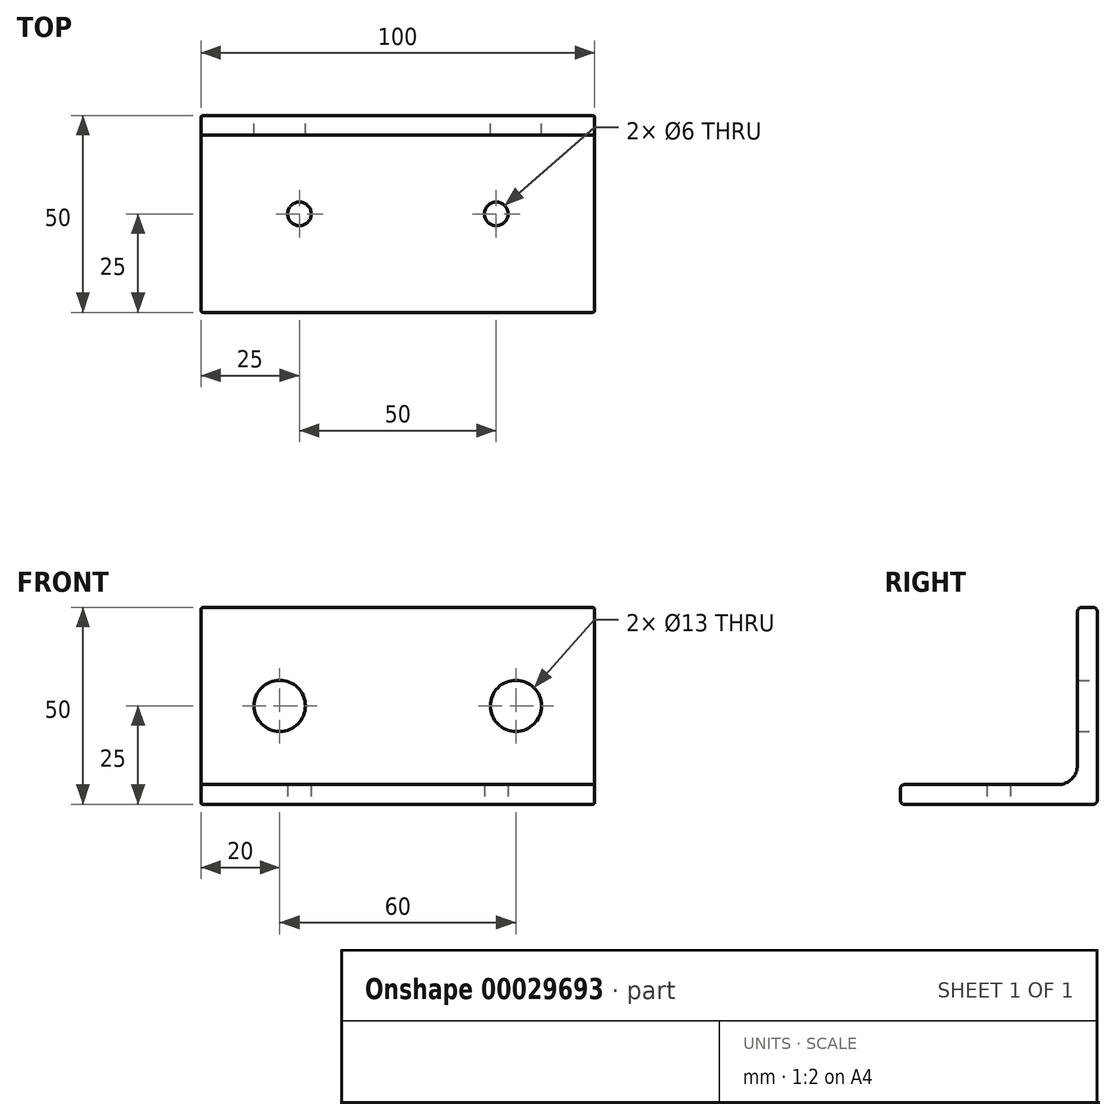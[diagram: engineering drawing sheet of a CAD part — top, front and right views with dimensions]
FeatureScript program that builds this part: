
annotation { "Feature Type Name" : "Feature", "Feature Type Description" : "" }
export const myFeature = defineFeature(function(context is Context, id is Id, definition is map)
    precondition{}
    {
        {
            var Q0;
            Q0=qCreatedBy(makeId("Right.planeOp"),FACE);
            var sketch = newSketch(context, id + "F0", { "sketchPlane" : qUnion([Q0])});
            skLineSegment(sketch, "E0", {"start": v(-49, 0) * mm, "end": v(-1, 0) * mm});
            skLineSegment(sketch, "E1", {"start": v(0, 1) * mm, "end": v(0, 49) * mm});
            skLineSegment(sketch, "E2", {"start": v(-1, 50) * mm, "end": v(-4, 50) * mm});
            skLineSegment(sketch, "E3", {"start": v(-5, 49) * mm, "end": v(-5, 10) * mm});
            skLineSegment(sketch, "E4", {"start": v(-10, 5) * mm, "end": v(-49, 5) * mm});
            skLineSegment(sketch, "E5", {"start": v(-50, 4) * mm, "end": v(-50, 1) * mm});
            skPoint(sketch, "E6.visualSharp", {"position": v(-5, 5) * mm});
            skArc(sketch, "E6.filletArc", {"start": v(-10, 5) * mm, "mid": v(-6.46, 6.46) * mm, "end": v(-5, 10) * mm});
            skPoint(sketch, "E7.visualSharp", {"position": v(0, 50) * mm});
            skArc(sketch, "E7.filletArc", {"start": v(0, 49) * mm, "mid": v(-0.3, 49.7) * mm, "end": v(-1, 50) * mm});
            skPoint(sketch, "E8.visualSharp", {"position": v(-5, 50) * mm});
            skArc(sketch, "E8.filletArc", {"start": v(-4, 50) * mm, "mid": v(-4.7, 49.7) * mm, "end": v(-5, 49) * mm});
            skPoint(sketch, "E9.visualSharp", {"position": v(-50, 5) * mm});
            skArc(sketch, "E9.filletArc", {"start": v(-49, 5) * mm, "mid": v(-49.7, 4.7) * mm, "end": v(-50, 4) * mm});
            skPoint(sketch, "E10.visualSharp", {"position": v(-50, 0) * mm});
            skArc(sketch, "E10.filletArc", {"start": v(-50, 1) * mm, "mid": v(-49.7, 0.3) * mm, "end": v(-49, 0) * mm});
            skPoint(sketch, "E11.visualSharp", {"position": v(0, 0) * mm});
            skArc(sketch, "E11.filletArc", {"start": v(-1, 0) * mm, "mid": v(-0.3, 0.3) * mm, "end": v(0, 1) * mm});
            skSolve(sketch);
        }
        {
            var Q0;
            Q0=qSketchRegion(id+"F0",true);
            extrude(context, id + "F1", {"entities" : qUnion([Q0]), "endBound" : BoundingType.SYMMETRIC, "depth" : 100 * mm});
        }
        {
            var Q0;
            Q0=makeQuery(id+"F1.opExtrude","SWEPT_FACE",FACE,{"disambiguationData":[OSD([sQuery(id+"F0.wireOp",EDGE,"E1")])]});
            var sketch = newSketch(context, id + "F2", { "sketchPlane" : qUnion([Q0])});
            skLineSegment(sketch, "E12.0", {"start": v(-50, 50) * mm, "end": v(50, 50) * mm, "construction": true});
            skLineSegment(sketch, "E12.1", {"start": v(-50, 0) * mm, "end": v(50, 0) * mm, "construction": true});
            skLineSegment(sketch, "E13", {"start": v(-50, 25) * mm, "end": v(-30, 25) * mm, "construction": true});
            skLineSegment(sketch, "E14", {"start": v(50, 25) * mm, "end": v(30, 25) * mm, "construction": true});
            skCircle(sketch, "E15", {"center": v(-30, 25) * mm, "radius": 6.5 * mm});
            skCircle(sketch, "E16", {"center": v(30, 25) * mm, "radius": 6.5 * mm});
            skSolve(sketch);
        }
        {
            var Q0;
            Q0=makeQuery(id+"F2.imprint","IMPRINT",FACE,{"disambiguationData":[TD([[makeQuery(id+"F2.imprint","IMPRINT",EDGE,{"derivedFrom":sQuery(id+"F2.wireOp",EDGE,"E15")}),1.0]])]});
            var Q1;
            Q1=makeQuery(id+"F2.imprint","IMPRINT",FACE,{"disambiguationData":[TD([[makeQuery(id+"F2.imprint","IMPRINT",EDGE,{"derivedFrom":sQuery(id+"F2.wireOp",EDGE,"E16")}),1.0]])]});
            extrude(context, id + "F3", {"entities" : qUnion([Q0, Q1]), "operationType" : NewBodyOperationType.REMOVE, "endBound" : BoundingType.THROUGH_ALL, "oppositeDirection" : true, "depth" : 25 * mm});
        }
        {
            var Q0;
            Q0=makeQuery(id+"F1.opExtrude","SWEPT_FACE",FACE,{"disambiguationData":[OSD([sQuery(id+"F0.wireOp",EDGE,"E0")])]});
            var sketch = newSketch(context, id + "F4", { "sketchPlane" : qUnion([Q0])});
            skLineSegment(sketch, "E17", {"start": v(50, 25) * mm, "end": v(25, 25) * mm, "construction": true});
            skLineSegment(sketch, "E18", {"start": v(-50, 25) * mm, "end": v(-25, 25) * mm, "construction": true});
            skCircle(sketch, "E19", {"center": v(25, 25) * mm, "radius": 3 * mm});
            skCircle(sketch, "E20", {"center": v(-25, 25) * mm, "radius": 3 * mm});
            skSolve(sketch);
        }
        {
            var Q0;
            Q0=makeQuery(id+"F4.imprint","IMPRINT",FACE,{"disambiguationData":[TD([[makeQuery(id+"F4.imprint","IMPRINT",EDGE,{"derivedFrom":sQuery(id+"F4.wireOp",EDGE,"E19")}),1.0]])]});
            var Q1;
            Q1=makeQuery(id+"F4.imprint","IMPRINT",FACE,{"disambiguationData":[TD([[makeQuery(id+"F4.imprint","IMPRINT",EDGE,{"derivedFrom":sQuery(id+"F4.wireOp",EDGE,"E20")}),1.0]])]});
            extrude(context, id + "F5", {"entities" : qUnion([Q0, Q1]), "operationType" : NewBodyOperationType.REMOVE, "endBound" : BoundingType.THROUGH_ALL, "oppositeDirection" : true, "depth" : 25 * mm});
        }
        {
            var Q0;
            Q0=makeQuery(id+"F1.opExtrude","CAP_EDGE",EDGE,{"disambiguationData":[OSD([sQuery(id+"F0.wireOp",EDGE,"E4")])],"isStart":false});
            var Q1;
            Q1=makeQuery(id+"F1.opExtrude","CAP_EDGE",EDGE,{"disambiguationData":[OSD([sQuery(id+"F0.wireOp",EDGE,"E4")])],"isStart":true});
            fillet(context, id + "F6", {"entities" : qUnion([Q0, Q1]), "radius" : 0.5 * mm, "tangentPropagation" : true, "allowEdgeOverflow" : false});
        }
    });
